# Revit family: НЕВАТОМ_Щит управления противодымной вентиляцией ABUm-PDV, Версия 1
name_source: partatom
category: Электрооборудование
revit_build: Autodesk Revit 2017 (Build: 20170118_1100(x64)
units: mm (PartAtom-declared; Revit-internal decimal feet)

## family parameters
Всегда вертикально = Да
Конфигурация панели = Два столбца, слева направо
На основе рабочей плоскости = Нет
Общий = Нет
При загрузке вырезать с полостями = Нет
Размер круглого соединителя = Использовать диаметр
Тип детали = Щит
Точка расчета площади = Нет

## types (60) — shared parameters
ADSK_Единица измерения = шт.
ADSK_Завод-изготовитель = НЕВАТОМ
ADSK_Количество = 1
ADSK_Напряжение = 220 В
ADSK_Размер_Высота = 800 мм
ADSK_Размер_Длина = 600 мм
ADSK_Размер_Ширина = 200 мм

## per-type parameters (varying)
| type | ADSK_Марка | ADSK_Наименование | НЕВАТОМ_Номинальный ток двигателя | НЕВАТОМ_Ориентировочная мощность двигателя |
| ABUm-PDV-0,37 | ABUm-PDV-0,37 | ABUm-PDV-0,37 | 1 А | 0 кВт |
| ABUm-PDV-0,55 | ABUm-PDV-0,55 | ABUm-PDV-0,55 | 2 А | 1 кВт |
| BUm-PDV-0,75 | BUm-PDV-0,75 | BUm-PDV-0,75 | 0 А | 0 кВт |
| ABUm-PDV-1,1 | ABUm-PDV-1,1 | ABUm-PDV-1,1 | 3 А | 1 кВт |
| ABUm-PDV-1,5 | ABUm-PDV-1,5 | ABUm-PDV-1,5 | 5 А | 2 кВт |
| BUm-PDV-2,2 | BUm-PDV-2,2 | BUm-PDV-2,2 | 6 А | 2 кВт |
| BUm-PDV-3,0 | BUm-PDV-3,0 | BUm-PDV-3,0 | 8 А | 3 кВт |
| ABUm-PDV-4,0 | ABUm-PDV-4,0 | ABUm-PDV-4,0 | 10 А | 4 кВт |
| ABUm-PDV-5,5 | ABUm-PDV-5,5 | ABUm-PDV-5,5 | 13 А | 6 кВт |
| BUm-PDV-7,5 | BUm-PDV-7,5 | BUm-PDV-7,5 | 18 А | 8 кВт |
| ABUm-PDV-11 | ABUm-PDV-11 | ABUm-PDV-11 | 25 А | 11 кВт |
| ABUm-PDV-15 | ABUm-PDV-15 | ABUm-PDV-15 | 33 А | 15 кВт |
| ABUm-PDV-18,5 | ABUm-PDV-18,5 | ABUm-PDV-18,5 | 39 А | 19 кВт |
| ABUm-PDV-22 | ABUm-PDV-22 | ABUm-PDV-22 | 46 А | 22 кВт |
| ABUm-PDV-30 | ABUm-PDV-30 | ABUm-PDV-30 | 62 А | 30 кВт |
| ABUm-PDV-0,37-MR220(24)/1 | ABUm-PDV-0,37-MR220(24)/1 | ABUm-PDV-0,37-MR220(24)/1 | 1 А | 0 кВт |
| ABUm-PDV-0,55-MR220(24)/1 | ABUm-PDV-0,55-MR220(24)/1 | ABUm-PDV-0,55-MR220(24)/1 | 1 А | 2 кВт |
| ABUm-PDV-0,75-MR220(24)/1 | ABUm-PDV-0,75-MR220(24)/1 | ABUm-PDV-0,75-MR220(24)/1 | 2 А | 1 кВт |
| ABUm-PDV-1,1-MR220(24)/1 | ABUm-PDV-1,1-MR220(24)/1 | ABUm-PDV-1,1-MR220(24)/1 | 3 А | 1 кВт |
| ABUm-PDV-1,5-MR220(24)/1 | ABUm-PDV-1,5-MR220(24)/1 | ABUm-PDV-1,5-MR220(24)/1 | 5 А | 2 кВт |
| ABUm-PDV-2,2-MR220(24)/1 | ABUm-PDV-1,5-MR220(24)/1 | ABUm-PDV-1,5-MR220(24)/1 | 6 А | 2 кВт |
| ABUm-PDV-3,0-MR220(24)/1 | ABUm-PDV-3,0-MR220(24)/1 | ABUm-PDV-3,0-MR220(24)/1 | 8 А | 3 кВт |
| ABUm-PDV-4,0-MR220(24)/1 | ABUm-PDV-4,0-MR220(24)/1 | ABUm-PDV-4,0-MR220(24)/1 | 10 А | 4 кВт |
| ABUm-PDV-5,5-MR220(24)/1 | ABUm-PDV-5,5-MR220(24)/1 | ABUm-PDV-5,5-MR220(24)/1 | 13 А | 6 кВт |
| ABUm-PDV-7,5-MR220(24)/1 | ABUm-PDV-7,5-MR220(24)/1 | ABUm-PDV-7,5-MR220(24)/1 | 18 А | 8 кВт |
| ABUm-PDV-11-MR220(24)/1 | ABUm-PDV-11-MR220(24)/1 | ABUm-PDV-11-MR220(24)/1 | 25 А | 11 кВт |
| ABUm-PDV-15-MR220(24)/1 | ABUm-PDV-15-MR220(24)/1 | ABUm-PDV-15-MR220(24)/1 | 33 А | 15 кВт |
| ABUm-PDV-18,5-MR220(24)/1 | ABUm-PDV-18,5-MR220(24)/1 | ABUm-PDV-18,5-MR220(24)/1 | 39 А | 19 кВт |
| ABUm-PDV-22-MR220(24)/1 | ABUm-PDV-22-MR220(24)/1 | ABUm-PDV-22-MR220(24)/1 | 46 А | 22 кВт |
| ABUm-PDV-30-MR220(24)/1 | ABUm-PDV-30-MR220(24)/1 | ABUm-PDV-30-MR220(24)/1 | 62 А | 30 кВт |
| ABUm-PDV-0,37-MP220(24)/1 | ABUm-PDV-0,37-MP220(24)/1 | ABUm-PDV-0,37-MP220(24)/1 | 1 А | 0 кВт |
| ABUm-PDV-0,55-MP220(24)/1 | ABUm-PDV-0,55-MP220(24)/1 | ABUm-PDV-0,55-MP220(24)/1 | 2 А | 1 кВт |
| ABUm-PDV-0,75-MP220(24)/1 | ABUm-PDV-0,75-MP220(24)/1 | ABUm-PDV-0,75-MP220(24)/1 | 2 А | 1 кВт |
| ABUm-PDV-1,1-MP220(24)/1 | ABUm-PDV-1,1-MP220(24)/1 | ABUm-PDV-1,1-MP220(24)/1 | 3 А | 1 кВт |
| ABUm-PDV-1,5-MP220(24)/1 | ABUm-PDV-1,5-MP220(24)/1 | ABUm-PDV-1,5-MP220(24)/1 | 5 А | 2 кВт |
| ABUm-PDV-2,2-MP220(24)/1 | ABUm-PDV-2,2-MP220(24)/1 | ABUm-PDV-2,2-MP220(24)/1 | 6 А | 2 кВт |
| ABUm-PDV-3,0-MP220(24)/1 | ABUm-PDV-3,0-MP220(24)/1 | ABUm-PDV-3,0-MP220(24)/1 | 8 А | 3 кВт |
| ABUm-PDV-4,0-MP220(24)/1 | ABUm-PDV-4,0-MP220(24)/1 | ABUm-PDV-4,0-MP220(24)/1 | 10 А | 4 кВт |
| ABUm-PDV-5,5-MP220(24)/1 | ABUm-PDV-5,5-MP220(24)/1 | ABUm-PDV-5,5-MP220(24)/1 | 13 А | 6 кВт |
| ABUm-PDV-7,5-MP220(24)/1 | ABUm-PDV-7,5-MP220(24)/1 | ABUm-PDV-7,5-MP220(24)/1 | 18 А | 8 кВт |
| ABUm-PDV-11-MP220(24)/1 | ABUm-PDV-11-MP220(24)/1 | ABUm-PDV-11-MP220(24)/1 | 0 А | 0 кВт |
| ABUm-PDV-15-MP220(24)/1 | ABUm-PDV-15-MP220(24)/1 | ABUm-PDV-15-MP220(24)/1 | 33 А | 15 кВт |
| ABUm-PDV-18,5-MP220(24)/1 | ABUm-PDV-18,5-MP220(24)/1 | ABUm-PDV-18,5-MP220(24)/1 | 39 А | 19 кВт |
| ABUm-PDV-22-MP220(24)/1 | ABUm-PDV-22-MP220(24)/1 | ABUm-PDV-22-MP220(24)/1 | 46 А | 22 кВт |
| ABUm-PDV-30-MP220(24)/1 | ABUm-PDV-30-MP220(24)/1 | ABUm-PDV-30-MP220(24)/1 | 62 А | 30 кВт |
| ABUm-PDV-0,37-EM220(24)/1 | ABUm-PDV-0,37-EM220(24)/1 | ABUm-PDV-0,37-EM220(24)/1 | 1 А | 0 кВт |
| ABUm-PDV-0,55-EM220(24)/1 | ABUm-PDV-0,55-EM220(24)/1 | ABUm-PDV-0,55-EM220(24)/1 | 2 А | 1 кВт |
| ABUm-PDV-0,75-EM220(24)/1 | ABUm-PDV-0,55-EM220(24)/1 | ABUm-PDV-0,55-EM220(24)/1 | 2 А | 1 кВт |
| ABUm-PDV-1,1-EM220(24)/1 | ABUm-PDV-0,55-EM220(24)/1 | ABUm-PDV-0,55-EM220(24)/1 | 3 А | 1 кВт |
| ABUm-PDV-1,5-EM220(24)/1 | ABUm-PDV-1,5-EM220(24)/1 | ABUm-PDV-1,5-EM220(24)/1 | 5 А | 2 кВт |
| ABUm-PDV-2,2-EM220(24)/1 | ABUm-PDV-2,2-EM220(24)/1 | ABUm-PDV-2,2-EM220(24)/1 | 6 А | 2 кВт |
| ABUm-PDV-3,0-EM220(24)/1 | ABUm-PDV-3,0-EM220(24)/1 | ABUm-PDV-3,0-EM220(24)/1 | 8 А | 3 кВт |
| ABUm-PDV-4,0-EM220(24)/1 | ABUm-PDV-4,0-EM220(24)/1 | ABUm-PDV-4,0-EM220(24)/1 | 0 А | 0 кВт |
| ABUm-PDV-5,5-EM220(24)/1 | ABUm-PDV-5,5-EM220(24)/1 | ABUm-PDV-5,5-EM220(24)/1 | 13 А | 6 кВт |
| ABUm-PDV-7,5-EM220(24)/1 | ABUm-PDV-7,5-EM220(24)/1 | ABUm-PDV-7,5-EM220(24)/1 | 18 А | 8 кВт |
| ABUm-PDV-11-EM220(24)/1 | ABUm-PDV-11-EM220(24)/1 | ABUm-PDV-11-EM220(24)/1 | 25 А | 11 кВт |
| ABUm-PDV-15-EM220(24)/1 | ABUm-PDV-15-EM220(24)/1 | ABUm-PDV-15-EM220(24)/1 | 33 А | 15 кВт |
| ABUm-PDV-18,5-EM220(24)/1 | ABUm-PDV-18,5-EM220(24)/1 | ABUm-PDV-18,5-EM220(24)/1 | 39 А | 19 кВт |
| ABUm-PDV-22-EM220(24)/1 | ABUm-PDV-22-EM220(24)/1 | ABUm-PDV-22-EM220(24)/1 | 46 А | 22 кВт |
| ABUm-PDV-30-EM220(24)/1 | ABUm-PDV-30-EM220(24)/1 | ABUm-PDV-30-EM220(24)/1 | 62 А | 30 кВт |
